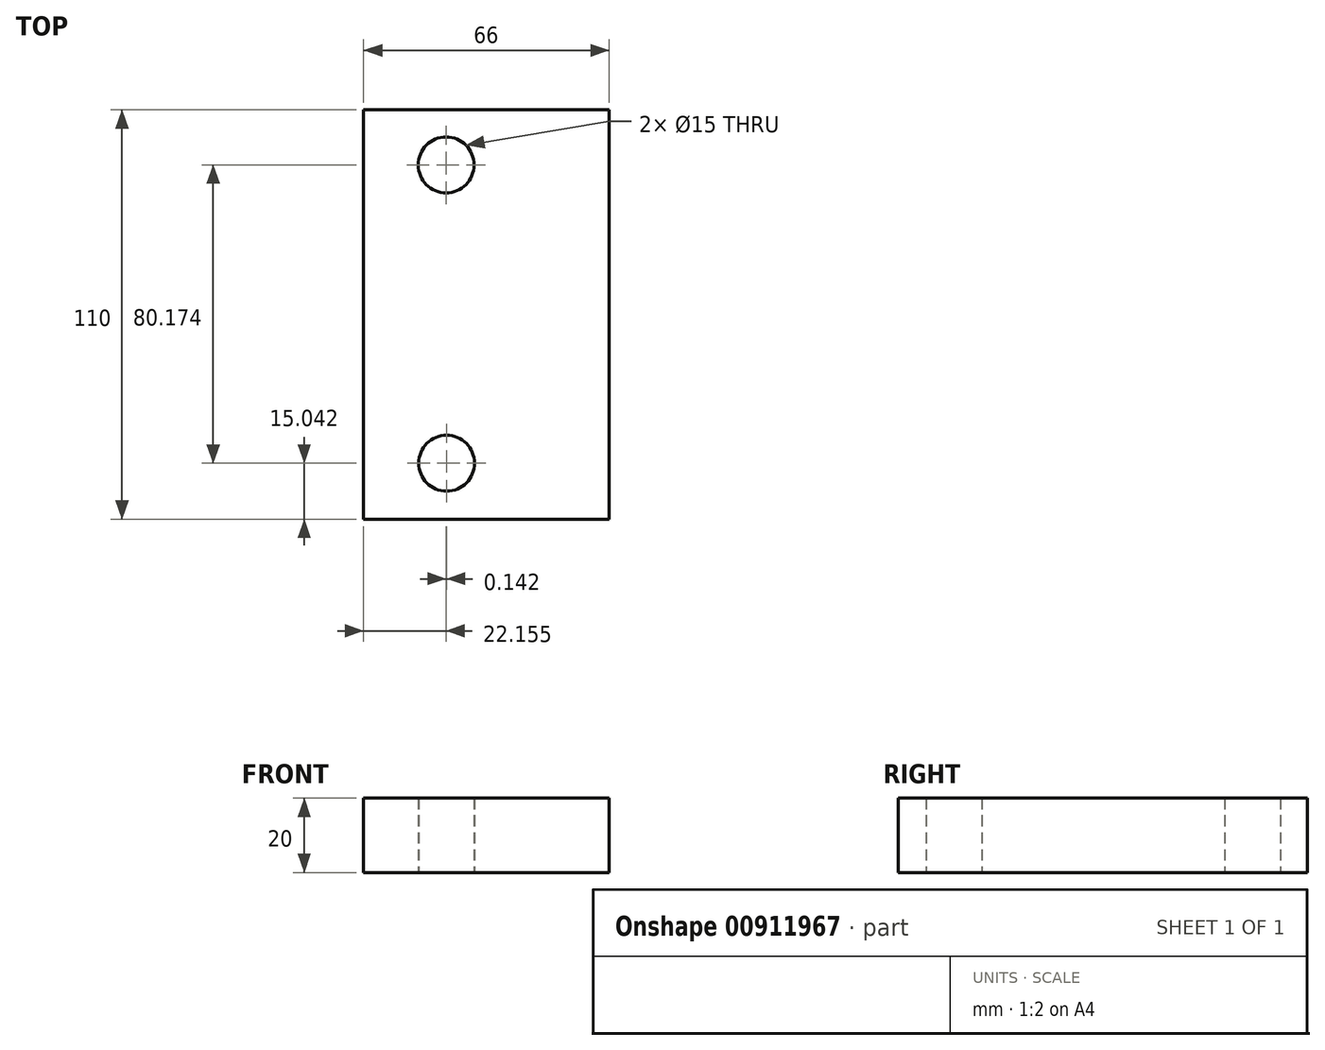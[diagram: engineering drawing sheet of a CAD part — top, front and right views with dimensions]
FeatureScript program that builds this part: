
annotation { "Feature Type Name" : "Feature", "Feature Type Description" : "" }
export const myFeature = defineFeature(function(context is Context, id is Id, definition is map)
    precondition{}
    {
        {
            var Q0;
            Q0=qCreatedBy(makeId("Top.planeOp"),FACE);
            var sketch = newSketch(context, id + "F0", { "sketchPlane" : qUnion([Q0])});
            skLineSegment(sketch, "E0", {"start": v(0, 0) * mm, "end": v(0, 55) * mm});
            skLineSegment(sketch, "E1", {"start": v(0, -55) * mm, "end": v(-66, -55) * mm});
            skLineSegment(sketch, "E2", {"start": v(0, 55) * mm, "end": v(-66, 55) * mm});
            skLineSegment(sketch, "E3", {"start": v(0, 0) * mm, "end": v(0, -55) * mm});
            skLineSegment(sketch, "E4", {"start": v(-66, 55) * mm, "end": v(-66, -55) * mm});
            skLineSegment(sketch, "E5.0", {"start": v(-44, 55) * mm, "end": v(-44, -55) * mm});
            skLineSegment(sketch, "E6.0", {"start": v(0, -40) * mm, "end": v(-66, -40) * mm});
            skLineSegment(sketch, "E7.0", {"start": v(0, 40) * mm, "end": v(-66, 40) * mm});
            skSolve(sketch);
        }
        {
            var Q0;
            {var subQ0=sQuery(id+"F0.wireOp",EDGE,"E4");var subQ1=sQuery(id+"F0.wireOp",EDGE,"E2");var subQ2=makeQuery(id+"F0.imprint","INTERSECT",VERTEX,{"derivedFrom":[subQ1,subQ0]});Q0=makeQuery(id+"F0.imprint","IMPRINT",FACE,{"disambiguationData":[TD([[makeQuery(id+"F0.imprint","IMPRINT",EDGE,{"disambiguationData":[TD([[subQ2,1.0]])],"derivedFrom":subQ1}),1.0]])]});}
            var Q1;
            {var subQ0=sQuery(id+"F0.wireOp",EDGE,"E2");var subQ1=sQuery(id+"F0.wireOp",EDGE,"E0");var subQ2=makeQuery(id+"F0.imprint","INTERSECT",VERTEX,{"derivedFrom":[subQ1,subQ0]});Q1=makeQuery(id+"F0.imprint","IMPRINT",FACE,{"disambiguationData":[TD([[makeQuery(id+"F0.imprint","IMPRINT",EDGE,{"disambiguationData":[TD([[subQ2,1.0]])],"derivedFrom":subQ1}),1.0]])]});}
            var Q2;
            {var subQ1=sQuery(id+"F0.wireOp",EDGE,"E3");var subQ7=sQuery(id+"F0.wireOp",EDGE,"E0");var subQ8=makeQuery(id+"F0.imprint","INTERSECT",VERTEX,{"derivedFrom":[subQ7,subQ1]});Q2=makeQuery(id+"F0.imprint","IMPRINT",FACE,{"disambiguationData":[TD([[makeQuery(id+"F0.imprint","IMPRINT",EDGE,{"disambiguationData":[TD([[subQ8,-1.0]])],"derivedFrom":subQ7}),1.0]])]});}
            var Q3;
            {var subQ0=sQuery(id+"F0.wireOp",EDGE,"E6.0");var subQ1=sQuery(id+"F0.wireOp",EDGE,"E4");var subQ2=makeQuery(id+"F0.imprint","INTERSECT",VERTEX,{"derivedFrom":[subQ1,subQ0]});Q3=makeQuery(id+"F0.imprint","IMPRINT",FACE,{"disambiguationData":[TD([[makeQuery(id+"F0.imprint","IMPRINT",EDGE,{"disambiguationData":[TD([[subQ2,1.0]])],"derivedFrom":subQ1}),1.0]])]});}
            var Q4;
            {var subQ0=sQuery(id+"F0.wireOp",EDGE,"E4");var subQ1=sQuery(id+"F0.wireOp",EDGE,"E1");var subQ2=makeQuery(id+"F0.imprint","INTERSECT",VERTEX,{"derivedFrom":[subQ1,subQ0]});Q4=makeQuery(id+"F0.imprint","IMPRINT",FACE,{"disambiguationData":[TD([[makeQuery(id+"F0.imprint","IMPRINT",EDGE,{"disambiguationData":[TD([[subQ2,1.0]])],"derivedFrom":subQ1}),-1.0]])]});}
            var Q5;
            {var subQ0=sQuery(id+"F0.wireOp",EDGE,"E3");var subQ1=sQuery(id+"F0.wireOp",EDGE,"E1");var subQ2=makeQuery(id+"F0.imprint","INTERSECT",VERTEX,{"derivedFrom":[subQ1,subQ0]});Q5=makeQuery(id+"F0.imprint","IMPRINT",FACE,{"disambiguationData":[TD([[makeQuery(id+"F0.imprint","IMPRINT",EDGE,{"disambiguationData":[TD([[subQ2,-1.0]])],"derivedFrom":subQ1}),-1.0]])]});}
            extrude(context, id + "F1", {"entities" : qUnion([Q0, Q1, Q2, Q3, Q4, Q5]), "depth" : 20 * mm, "offsetDistance" : 25 * mm});
        }
        {
            var Q0;
            {var subQ1=sQuery(id+"F0.wireOp",EDGE,"E3");var subQ7=sQuery(id+"F0.wireOp",EDGE,"E0");var subQ8=makeQuery(id+"F0.imprint","INTERSECT",VERTEX,{"derivedFrom":[subQ7,subQ1]});Q0=makeQuery(id+"F0.imprint","IMPRINT",FACE,{"disambiguationData":[TD([[makeQuery(id+"F0.imprint","IMPRINT",EDGE,{"disambiguationData":[TD([[subQ8,-1.0]])],"derivedFrom":subQ7}),1.0]])]});}
            var sketch = newSketch(context, id + "F2", { "sketchPlane" : qUnion([Q0])});
            skPoint(sketch, "E8", {"position": v(-43.7, -39.96) * mm});
            skPoint(sketch, "E9", {"position": v(-43.84, 40.22) * mm});
            skSolve(sketch);
        }
        {
            var Q0;
            Q0=sQuery(id+"F2.wireOp",VERTEX,"E9");
            var Q1;
            Q1=sQuery(id+"F2.wireOp",VERTEX,"E8");
            var Q2;
            Q2=makeQuery(id+"F1.opExtrude","SWEPT_BODY",BODY,{"disambiguationData":[OSD([sQuery(id+"F0.wireOp",EDGE,"E0"),sQuery(id+"F0.wireOp",EDGE,"E1"),sQuery(id+"F0.wireOp",EDGE,"E2"),sQuery(id+"F0.wireOp",EDGE,"E3"),sQuery(id+"F0.wireOp",EDGE,"E4")])]});
            hole(context, id + "F3", {"style" : HoleStyle.SIMPLE, "endStyle" : HoleEndStyle.THROUGH, "oppositeDirection" : true, "holeDiameter" : 15 * mm, "majorDiameter" : 5 * mm, "isTappedThrough" : true, "tappedDepth" : 12 * mm, "tapClearance" : 3, "locations" : qUnion([Q0, Q1]), "scope" : qUnion([Q2])});
        }
    });
